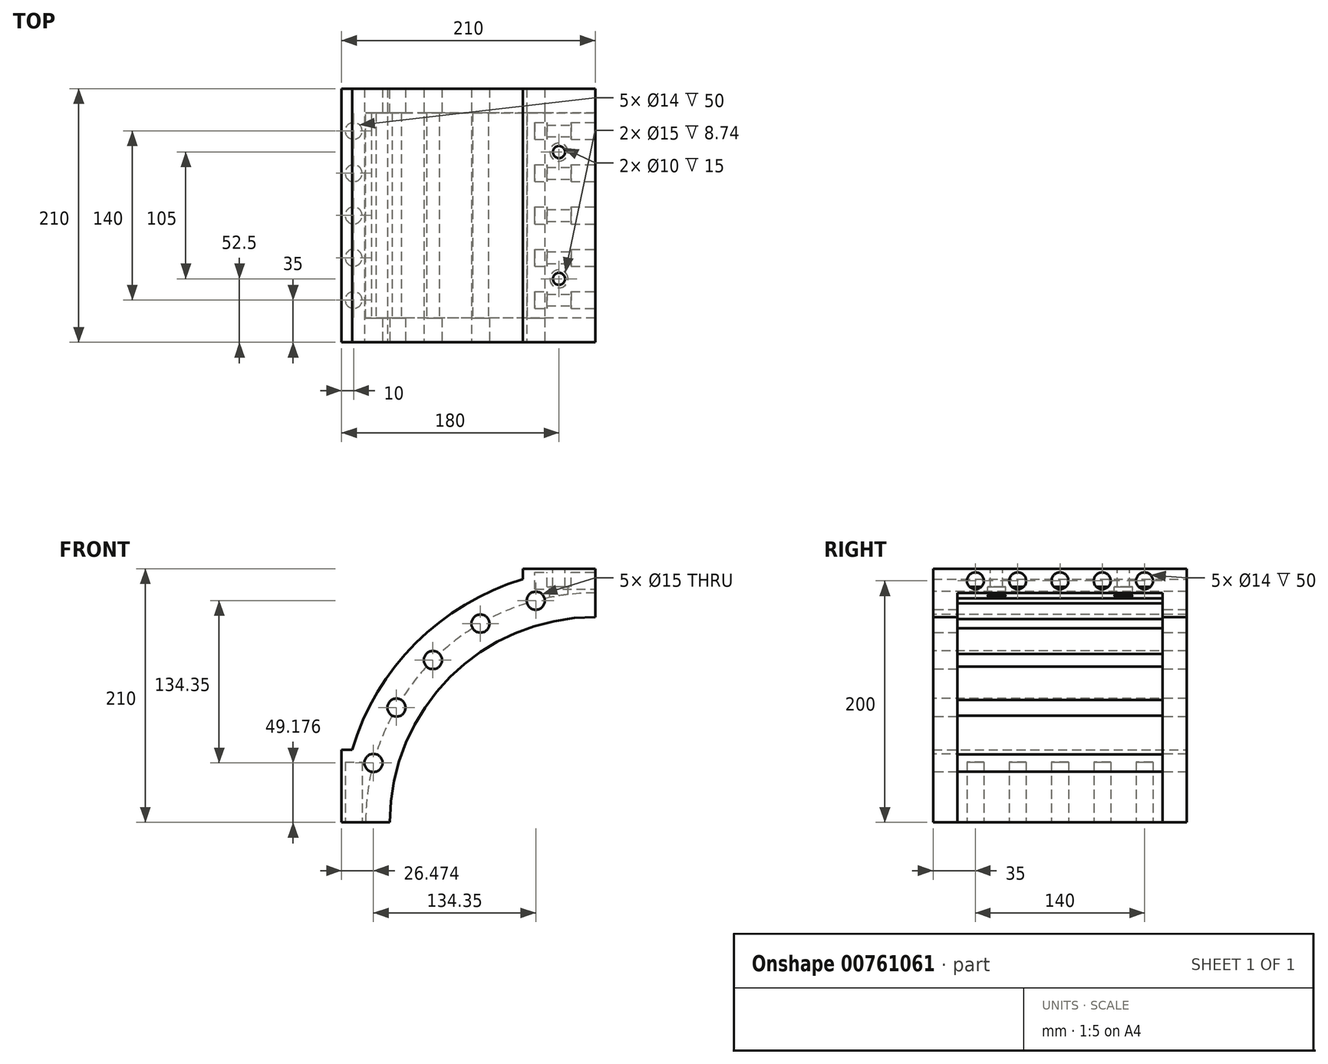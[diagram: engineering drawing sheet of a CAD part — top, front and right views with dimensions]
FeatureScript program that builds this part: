
annotation { "Feature Type Name" : "Feature", "Feature Type Description" : "" }
export const myFeature = defineFeature(function(context is Context, id is Id, definition is map)
    precondition{}
    {
        {
            var Q0;
            Q0=qCreatedBy(makeId("Front.planeOp"),FACE);
            var sketch = newSketch(context, id + "F0", { "sketchPlane" : qUnion([Q0])});
            skCircle(sketch, "E0", {"center": v(0, 0) * mm, "radius": 210 * mm});
            skCircle(sketch, "E1", {"center": v(0, 0) * mm, "radius": 190 * mm});
            skLineSegment(sketch, "E2.bottom", {"start": v(-210, 210) * mm, "end": v(210, 210) * mm});
            skLineSegment(sketch, "E2.top", {"start": v(-210, -210) * mm, "end": v(210, -210) * mm});
            skLineSegment(sketch, "E2.left", {"start": v(-210, 210) * mm, "end": v(-210, -210) * mm});
            skLineSegment(sketch, "E2.right", {"start": v(210, 210) * mm, "end": v(210, -210) * mm});
            skLineSegment(sketch, "E3", {"start": v(0, 210) * mm, "end": v(0, 0) * mm});
            skLineSegment(sketch, "E4", {"start": v(-210, 0) * mm, "end": v(0, 0) * mm});
            skSolve(sketch);
        }
        {
            var Q0;
            {var subQ0=sQuery(id+"F0.wireOp",EDGE,"E3");var subQ5=sQuery(id+"F0.wireOp",EDGE,"E1");var subQ7=makeQuery(id+"F0.imprint","INTERSECT",VERTEX,{"derivedFrom":[subQ5,subQ0]});Q0=makeQuery(id+"F0.imprint","IMPRINT",FACE,{"disambiguationData":[TD([[makeQuery(id+"F0.imprint","IMPRINT",EDGE,{"disambiguationData":[TD([[subQ7,-1.0]])],"derivedFrom":subQ5}),-1.0]])]});}
            extrude(context, id + "F1", {"entities" : qUnion([Q0]), "depth" : 210 * mm, "offsetDistance" : 25 * mm});
        }
        {
            var Q0;
            Q0=makeQuery(id+"F1.opExtrude","SWEPT_FACE",FACE,{"disambiguationData":[OSD([sQuery(id+"F0.wireOp",EDGE,"E3")])]});
            var sketch = newSketch(context, id + "F2", { "sketchPlane" : qUnion([Q0])});
            skSolve(sketch);
        }
        {
            var Q0;
            Q0 = qSketchRegion(id + "F2", true);
            var Q1;
            {var subQ0=sQuery(id+"F0.wireOp",EDGE,"E3");Q1=makeQuery(id+"F2.imprint","IMPRINT",FACE,{"disambiguationData":[TD([[makeQuery(id+"F2.imprint","IMPRINT",EDGE,{"derivedFrom":makeQuery(id+"F1.opExtrude","CAP_EDGE",EDGE,{"disambiguationData":[OSD([subQ0])],"isStart":true})}),-1.0]])]});}
            extrude(context, id + "F3", {"entities" : qUnion([Q0, Q1]), "operationType" : NewBodyOperationType.ADD, "oppositeDirection" : true, "depth" : 60 * mm, "offsetDistance" : 25 * mm});
        }
        {
            var Q0;
            Q0=makeQuery(id+"F1.opExtrude","SWEPT_FACE",FACE,{"disambiguationData":[OSD([sQuery(id+"F0.wireOp",EDGE,"E4")])]});
            extrude(context, id + "F4", {"entities" : qUnion([Q0]), "operationType" : NewBodyOperationType.ADD, "oppositeDirection" : true, "depth" : 60 * mm, "offsetDistance" : 25 * mm});
        }
        {
            var Q0;
            Q0=makeQuery(id+"F1.opExtrude","SWEPT_FACE",FACE,{"disambiguationData":[OSD([sQuery(id+"F0.wireOp",EDGE,"E3")])]});
            var sketch = newSketch(context, id + "F5", { "sketchPlane" : qUnion([Q0])});
            skLineSegment(sketch, "E5", {"start": v(-210, 200) * mm, "end": v(0, 200) * mm, "construction": true});
            skLineSegment(sketch, "E6", {"start": v(-105, 210) * mm, "end": v(-105, 190) * mm, "construction": true});
            skLineSegment(sketch, "E7", {"start": v(-175, 210) * mm, "end": v(-175, 190) * mm, "construction": true});
            skLineSegment(sketch, "E8", {"start": v(-140, 210) * mm, "end": v(-140, 190) * mm, "construction": true});
            skLineSegment(sketch, "E9", {"start": v(-70, 210) * mm, "end": v(-70, 190) * mm, "construction": true});
            skLineSegment(sketch, "E10", {"start": v(-35, 210) * mm, "end": v(-35, 190) * mm, "construction": true});
            skCircle(sketch, "E11", {"center": v(-175, 200) * mm, "radius": 7 * mm});
            skCircle(sketch, "E12", {"center": v(-140, 200) * mm, "radius": 7 * mm});
            skCircle(sketch, "E13", {"center": v(-105, 200) * mm, "radius": 7 * mm});
            skCircle(sketch, "E14", {"center": v(-70, 200) * mm, "radius": 7 * mm});
            skCircle(sketch, "E15", {"center": v(-35, 200) * mm, "radius": 7 * mm});
            skSolve(sketch);
        }
        {
            var Q0;
            Q0=makeQuery(id+"F5.imprint","IMPRINT",FACE,{"disambiguationData":[TD([[makeQuery(id+"F5.imprint","IMPRINT",EDGE,{"derivedFrom":sQuery(id+"F5.wireOp",EDGE,"E11")}),1.0]])]});
            var Q1;
            Q1=makeQuery(id+"F5.imprint","IMPRINT",FACE,{"disambiguationData":[TD([[makeQuery(id+"F5.imprint","IMPRINT",EDGE,{"derivedFrom":sQuery(id+"F5.wireOp",EDGE,"E12")}),1.0]])]});
            var Q2;
            Q2=makeQuery(id+"F5.imprint","IMPRINT",FACE,{"disambiguationData":[TD([[makeQuery(id+"F5.imprint","IMPRINT",EDGE,{"derivedFrom":sQuery(id+"F5.wireOp",EDGE,"E13")}),1.0]])]});
            var Q3;
            Q3=makeQuery(id+"F5.imprint","IMPRINT",FACE,{"disambiguationData":[TD([[makeQuery(id+"F5.imprint","IMPRINT",EDGE,{"derivedFrom":sQuery(id+"F5.wireOp",EDGE,"E14")}),1.0]])]});
            var Q4;
            Q4=makeQuery(id+"F5.imprint","IMPRINT",FACE,{"disambiguationData":[TD([[makeQuery(id+"F5.imprint","IMPRINT",EDGE,{"derivedFrom":sQuery(id+"F5.wireOp",EDGE,"E15")}),1.0]])]});
            var Q5;
            Q5 = qSketchRegion(id + "F7", true);
            extrude(context, id + "F6", {"entities" : qUnion([Q0, Q1, Q2, Q3, Q4, Q5]), "operationType" : NewBodyOperationType.REMOVE, "oppositeDirection" : true, "depth" : 50 * mm, "offsetDistance" : 25 * mm});
        }
        {
            var Q0;
            Q0=makeQuery(id+"F3.opExtrude","SWEPT_FACE",FACE,{"disambiguationData":[OSD([sQuery(id+"F0.wireOp",EDGE,"E0"),sQuery(id+"F0.wireOp",EDGE,"E2.bottom"),sQuery(id+"F0.wireOp",EDGE,"E3")])]});
            var sketch = newSketch(context, id + "F7", { "sketchPlane" : qUnion([Q0])});
            skLineSegment(sketch, "E16", {"start": v(-30, -210) * mm, "end": v(-30, 0) * mm});
            skLineSegment(sketch, "E17", {"start": v(-60, -157.5) * mm, "end": v(0, -157.5) * mm});
            skLineSegment(sketch, "E18", {"start": v(-60, -52.5) * mm, "end": v(0, -52.5) * mm});
            skLineSegment(sketch, "E19", {"start": v(-60, -105) * mm, "end": v(0, -105) * mm});
            skPoint(sketch, "E20", {"position": v(-30, -157.5) * mm});
            skPoint(sketch, "E21", {"position": v(-30, -105) * mm});
            skPoint(sketch, "E22", {"position": v(-30, -52.5) * mm});
            skSolve(sketch);
        }
        {
            var Q0;
            Q0=sQuery(id+"F7.wireOp",VERTEX,"E20");
            var Q1;
            Q1=sQuery(id+"F7.wireOp",VERTEX,"E22");
            var Q2;
            Q2=makeQuery(id+"F1.opExtrude","SWEPT_BODY",BODY,{"disambiguationData":[OSD([sQuery(id+"F0.wireOp",EDGE,"E0"),sQuery(id+"F0.wireOp",EDGE,"E1"),sQuery(id+"F0.wireOp",EDGE,"E3"),sQuery(id+"F0.wireOp",EDGE,"E4")])]});
            hole(context, id + "F8", {"style" : HoleStyle.SIMPLE, "endStyle" : HoleEndStyle.BLIND, "holeDiameter" : 15 * mm, "majorDiameter" : 5 * mm, "holeDepth" : 40 * mm, "isTappedThrough" : true, "tappedDepth" : 12 * mm, "tapClearance" : 3, "startFromSketch" : true, "locations" : qUnion([Q0, Q1]), "scope" : qUnion([Q2])});
        }
        {
            var Q0;
            {var subQ0=sQuery(id+"F0.wireOp",EDGE,"E4");var subQ1=sQuery(id+"F0.wireOp",EDGE,"E3");Q0=makeQuery(id+"F4.boolean.opBoolean","MERGE",FACE,{"derivedFrom":[makeQuery(id+"F3.boolean.opBoolean","MERGE",FACE,{"derivedFrom":[makeQuery(id+"F1.opExtrude","CAP_FACE",FACE,{"disambiguationData":[OSD([sQuery(id+"F0.wireOp",EDGE,"E0"),sQuery(id+"F0.wireOp",EDGE,"E1"),subQ1,subQ0])],"isStart":false}),makeQuery(id+"F3.opExtrude","SWEPT_FACE",FACE,{"disambiguationData":[OSD([subQ1]),TDD([makeQuery(id+"F2.imprint","IMPRINT",EDGE,{"derivedFrom":makeQuery(id+"F1.opExtrude","CAP_EDGE",EDGE,{"disambiguationData":[OSD([subQ1])],"isStart":false})})])]})]}),makeQuery(id+"F4.opExtrude","SWEPT_FACE",FACE,{"disambiguationData":[OSD([subQ0]),TDD([makeQuery(id+"F1.opExtrude","CAP_EDGE",EDGE,{"disambiguationData":[OSD([subQ0])],"isStart":false})])]})]});}
            var sketch = newSketch(context, id + "F9", { "sketchPlane" : qUnion([Q0])});
            skLineSegment(sketch, "E23", {"start": v(0, 0) * mm, "end": v(-200, 0) * mm, "construction": true});
            skCircle(sketch, "E24", {"center": v(0, 0) * mm, "radius": 170 * mm});
            skLineSegment(sketch, "E25", {"start": v(0, 0) * mm, "end": v(0, 190) * mm, "construction": true});
            skLineSegment(sketch, "E26", {"start": v(0, 190) * mm, "end": v(0, 170) * mm});
            skLineSegment(sketch, "E27", {"start": v(-190, 0) * mm, "end": v(-170, 0) * mm});
            skSolve(sketch);
        }
        {
            var Q0;
            {var subQ0=sQuery(id+"F9.wireOp",EDGE,"E26");Q0=makeQuery(id+"F9.imprint","IMPRINT",FACE,{"disambiguationData":[TD([[makeQuery(id+"F9.imprint","IMPRINT",EDGE,{"derivedFrom":subQ0}),-1.0]])]});}
            extrude(context, id + "F10", {"entities" : qUnion([Q0]), "operationType" : NewBodyOperationType.ADD, "oppositeDirection" : true, "depth" : 20 * mm, "offsetDistance" : 25 * mm});
        }
        {
            var Q0;
            {var subQ0=sQuery(id+"F0.wireOp",EDGE,"E4");var subQ1=sQuery(id+"F0.wireOp",EDGE,"E3");Q0=makeQuery(id+"F4.boolean.opBoolean","MERGE",FACE,{"derivedFrom":[makeQuery(id+"F3.boolean.opBoolean","MERGE",FACE,{"derivedFrom":[makeQuery(id+"F1.opExtrude","CAP_FACE",FACE,{"disambiguationData":[OSD([sQuery(id+"F0.wireOp",EDGE,"E0"),sQuery(id+"F0.wireOp",EDGE,"E1"),subQ1,subQ0])],"isStart":true}),makeQuery(id+"F3.opExtrude","SWEPT_FACE",FACE,{"disambiguationData":[OSD([subQ1]),TDD([makeQuery(id+"F2.imprint","IMPRINT",EDGE,{"derivedFrom":makeQuery(id+"F1.opExtrude","CAP_EDGE",EDGE,{"disambiguationData":[OSD([subQ1])],"isStart":true})})])]})]}),makeQuery(id+"F4.opExtrude","SWEPT_FACE",FACE,{"disambiguationData":[OSD([subQ0]),TDD([makeQuery(id+"F1.opExtrude","CAP_EDGE",EDGE,{"disambiguationData":[OSD([subQ0])],"isStart":true})])]})]});}
            var sketch = newSketch(context, id + "F11", { "sketchPlane" : qUnion([Q0])});
            skCircle(sketch, "E28", {"center": v(0, 0) * mm, "radius": 170 * mm});
            skLineSegment(sketch, "E29", {"start": v(0, 190) * mm, "end": v(0, 170) * mm});
            skLineSegment(sketch, "E30", {"start": v(190, 0) * mm, "end": v(170, 0) * mm});
            skSolve(sketch);
        }
        {
            var Q0;
            {var subQ0=sQuery(id+"F11.wireOp",EDGE,"E29");Q0=makeQuery(id+"F11.imprint","IMPRINT",FACE,{"disambiguationData":[TD([[makeQuery(id+"F11.imprint","IMPRINT",EDGE,{"derivedFrom":subQ0}),1.0]])]});}
            extrude(context, id + "F12", {"entities" : qUnion([Q0]), "operationType" : NewBodyOperationType.ADD, "oppositeDirection" : true, "depth" : 20 * mm, "offsetDistance" : 25 * mm});
        }
        {
            var Q0;
            {var subQ0=sQuery(id+"F0.wireOp",EDGE,"E1");var subQ1=sQuery(id+"F0.wireOp",EDGE,"E4");var subQ2=sQuery(id+"F0.wireOp",EDGE,"E3");Q0=makeQuery(id+"F10.boolean.opBoolean","MERGE",FACE,{"derivedFrom":[makeQuery(id+"F4.boolean.opBoolean","MERGE",FACE,{"derivedFrom":[makeQuery(id+"F3.boolean.opBoolean","MERGE",FACE,{"derivedFrom":[makeQuery(id+"F1.opExtrude","CAP_FACE",FACE,{"disambiguationData":[OSD([sQuery(id+"F0.wireOp",EDGE,"E0"),subQ0,subQ2,subQ1])],"isStart":false}),makeQuery(id+"F3.opExtrude","SWEPT_FACE",FACE,{"disambiguationData":[OSD([subQ2]),TDD([makeQuery(id+"F2.imprint","IMPRINT",EDGE,{"derivedFrom":makeQuery(id+"F1.opExtrude","CAP_EDGE",EDGE,{"disambiguationData":[OSD([subQ2])],"isStart":false})})])]})]}),makeQuery(id+"F4.opExtrude","SWEPT_FACE",FACE,{"disambiguationData":[OSD([subQ1]),TDD([makeQuery(id+"F1.opExtrude","CAP_EDGE",EDGE,{"disambiguationData":[OSD([subQ1])],"isStart":false})])]})]}),makeQuery(id+"F10.opExtrude","CAP_FACE",FACE,{"disambiguationData":[OSD([subQ0,sQuery(id+"F9.wireOp",EDGE,"E24"),sQuery(id+"F9.wireOp",EDGE,"E26"),sQuery(id+"F9.wireOp",EDGE,"E27")])],"isStart":true})]});}
            var sketch = newSketch(context, id + "F13", { "sketchPlane" : qUnion([Q0])});
            skPoint(sketch, "E31", {"position": v(0, 190) * mm});
            skCircle(sketch, "E32", {"center": v(0, 0) * mm, "radius": 190 * mm});
            skLineSegment(sketch, "E33", {"start": v(0, 0) * mm, "end": v(0, 190) * mm, "construction": true});
            skLineSegment(sketch, "E34", {"start": v(0, 0) * mm, "end": v(-190, 0) * mm, "construction": true});
            skLineSegment(sketch, "E35", {"start": v(0, 0) * mm, "end": v(-164.54, 95) * mm, "construction": true});
            skLineSegment(sketch, "E36", {"start": v(0, 0) * mm, "end": v(-95, 164.54) * mm, "construction": true});
            skLineSegment(sketch, "E37", {"start": v(0, 0) * mm, "end": v(-49.18, 183.53) * mm, "construction": true});
            skLineSegment(sketch, "E38", {"start": v(0, 0) * mm, "end": v(-183.53, 49.18) * mm, "construction": true});
            skLineSegment(sketch, "E39", {"start": v(0, 0) * mm, "end": v(-134.35, 134.35) * mm, "construction": true});
            skPoint(sketch, "E40", {"position": v(-49.18, 183.53) * mm});
            skPoint(sketch, "E41", {"position": v(-95, 164.54) * mm});
            skPoint(sketch, "E42", {"position": v(-134.35, 134.35) * mm});
            skPoint(sketch, "E43", {"position": v(-164.54, 95) * mm});
            skPoint(sketch, "E44", {"position": v(-183.53, 49.18) * mm});
            skSolve(sketch);
        }
        {
            var Q0;
            Q0=sQuery(id+"F13.wireOp",VERTEX,"E44");
            var Q1;
            Q1=sQuery(id+"F13.wireOp",VERTEX,"E43");
            var Q2;
            Q2=sQuery(id+"F13.wireOp",VERTEX,"E42");
            var Q3;
            Q3=sQuery(id+"F13.wireOp",VERTEX,"E41");
            var Q4;
            Q4=sQuery(id+"F13.wireOp",VERTEX,"E40");
            var Q5;
            Q5=makeQuery(id+"F1.opExtrude","SWEPT_BODY",BODY,{"disambiguationData":[OSD([sQuery(id+"F0.wireOp",EDGE,"E0"),sQuery(id+"F0.wireOp",EDGE,"E1"),sQuery(id+"F0.wireOp",EDGE,"E3"),sQuery(id+"F0.wireOp",EDGE,"E4")])]});
            hole(context, id + "F14", {"style" : HoleStyle.SIMPLE, "endStyle" : HoleEndStyle.BLIND, "holeDiameter" : 15 * mm, "majorDiameter" : 5 * mm, "holeDepth" : 220 * mm, "isTappedThrough" : true, "tappedDepth" : 12 * mm, "tapClearance" : 3, "startFromSketch" : true, "locations" : qUnion([Q0, Q1, Q2, Q3, Q4]), "scope" : qUnion([Q5])});
        }
        {
            var Q0;
            {var subQ0=sQuery(id+"F0.wireOp",EDGE,"E1");var subQ1=sQuery(id+"F0.wireOp",EDGE,"E4");var subQ2=sQuery(id+"F0.wireOp",EDGE,"E3");Q0=makeQuery(id+"F12.boolean.opBoolean","MERGE",FACE,{"derivedFrom":[makeQuery(id+"F4.boolean.opBoolean","MERGE",FACE,{"derivedFrom":[makeQuery(id+"F3.boolean.opBoolean","MERGE",FACE,{"derivedFrom":[makeQuery(id+"F1.opExtrude","CAP_FACE",FACE,{"disambiguationData":[OSD([sQuery(id+"F0.wireOp",EDGE,"E0"),subQ0,subQ2,subQ1])],"isStart":true}),makeQuery(id+"F3.opExtrude","SWEPT_FACE",FACE,{"disambiguationData":[OSD([subQ2]),TDD([makeQuery(id+"F2.imprint","IMPRINT",EDGE,{"derivedFrom":makeQuery(id+"F1.opExtrude","CAP_EDGE",EDGE,{"disambiguationData":[OSD([subQ2])],"isStart":true})})])]})]}),makeQuery(id+"F4.opExtrude","SWEPT_FACE",FACE,{"disambiguationData":[OSD([subQ1]),TDD([makeQuery(id+"F1.opExtrude","CAP_EDGE",EDGE,{"disambiguationData":[OSD([subQ1])],"isStart":true})])]})]}),makeQuery(id+"F12.opExtrude","CAP_FACE",FACE,{"disambiguationData":[OSD([subQ0,sQuery(id+"F11.wireOp",EDGE,"E28"),sQuery(id+"F11.wireOp",EDGE,"E29"),sQuery(id+"F11.wireOp",EDGE,"E30")])],"isStart":true})]});}
            var sketch = newSketch(context, id + "F15", { "sketchPlane" : qUnion([Q0])});
            skLineSegment(sketch, "E45", {"start": v(30, 210) * mm, "end": v(30, 167.33) * mm, "construction": true});
            skLineSegment(sketch, "E46", {"start": v(20, 210) * mm, "end": v(20, 168.82) * mm});
            skLineSegment(sketch, "E47", {"start": v(40, 210) * mm, "end": v(40, 165.23) * mm});
            skLineSegment(sketch, "E48", {"start": v(20, 190) * mm, "end": v(40, 190) * mm});
            skLineSegment(sketch, "E49", {"start": v(40, 195) * mm, "end": v(20, 195) * mm});
            skSolve(sketch);
        }
        {
            var Q0;
            {var subQ6=sQuery(id+"F15.wireOp",EDGE,"E49");Q0=makeQuery(id+"F15.imprint","IMPRINT",FACE,{"disambiguationData":[TD([[makeQuery(id+"F15.imprint","IMPRINT",EDGE,{"derivedFrom":subQ6}),-1.0]])]});}
            extrude(context, id + "F16", {"entities" : qUnion([Q0]), "operationType" : NewBodyOperationType.ADD, "oppositeDirection" : true, "depth" : 200 * mm, "offsetDistance" : 25 * mm});
        }
        {
            var Q0;
            Q0=sQuery(id+"F7.wireOp",VERTEX,"E22");
            var Q1;
            Q1=sQuery(id+"F7.wireOp",VERTEX,"E20");
            var Q2;
            Q2=makeQuery(id+"F1.opExtrude","SWEPT_BODY",BODY,{"disambiguationData":[OSD([sQuery(id+"F0.wireOp",EDGE,"E0"),sQuery(id+"F0.wireOp",EDGE,"E1"),sQuery(id+"F0.wireOp",EDGE,"E3"),sQuery(id+"F0.wireOp",EDGE,"E4")])]});
            hole(context, id + "F17", {"style" : HoleStyle.SIMPLE, "endStyle" : HoleEndStyle.BLIND, "holeDiameter" : 10 * mm, "majorDiameter" : 5 * mm, "holeDepth" : 40 * mm, "isTappedThrough" : true, "tappedDepth" : 12 * mm, "tapClearance" : 3, "startFromSketch" : true, "locations" : qUnion([Q0, Q1]), "scope" : qUnion([Q2])});
        }
        {
            var Q0;
            Q0=makeQuery(id+"F12.boolean.opBoolean","MERGE",FACE,{"derivedFrom":[makeQuery(id+"F10.boolean.opBoolean","MERGE",FACE,{"derivedFrom":[makeQuery(id+"F1.opExtrude","SWEPT_FACE",FACE,{"disambiguationData":[OSD([sQuery(id+"F0.wireOp",EDGE,"E4")])]}),makeQuery(id+"F10.opExtrude","SWEPT_FACE",FACE,{"disambiguationData":[OSD([sQuery(id+"F9.wireOp",EDGE,"E27")])]})]}),makeQuery(id+"F12.opExtrude","SWEPT_FACE",FACE,{"disambiguationData":[OSD([sQuery(id+"F11.wireOp",EDGE,"E30")])]})]});
            var sketch = newSketch(context, id + "F18", { "sketchPlane" : qUnion([Q0])});
            skLineSegment(sketch, "E50", {"start": v(-190, 105) * mm, "end": v(-210, 105) * mm, "construction": true});
            skLineSegment(sketch, "E51", {"start": v(-200, 105) * mm, "end": v(-200, 210) * mm, "construction": true});
            skLineSegment(sketch, "E52", {"start": v(-200, 105) * mm, "end": v(-200, 0) * mm, "construction": true});
            skLineSegment(sketch, "E53", {"start": v(-210, 35) * mm, "end": v(-190, 35) * mm, "construction": true});
            skLineSegment(sketch, "E54", {"start": v(-210, 70) * mm, "end": v(-190, 70) * mm, "construction": true});
            skLineSegment(sketch, "E55", {"start": v(-210, 175) * mm, "end": v(-190, 175) * mm, "construction": true});
            skLineSegment(sketch, "E56", {"start": v(-210, 140) * mm, "end": v(-190, 140) * mm, "construction": true});
            skPoint(sketch, "E57", {"position": v(-200, 35) * mm});
            skPoint(sketch, "E58", {"position": v(-200, 70) * mm});
            skPoint(sketch, "E59", {"position": v(-200, 105) * mm});
            skPoint(sketch, "E60", {"position": v(-200, 140) * mm});
            skPoint(sketch, "E61", {"position": v(-200, 175) * mm});
            skCircle(sketch, "E62", {"center": v(-200, 35) * mm, "radius": 7 * mm});
            skCircle(sketch, "E63", {"center": v(-200, 70) * mm, "radius": 7 * mm});
            skCircle(sketch, "E64", {"center": v(-200, 105) * mm, "radius": 7 * mm});
            skCircle(sketch, "E65", {"center": v(-200, 140) * mm, "radius": 7 * mm});
            skCircle(sketch, "E66", {"center": v(-200, 175) * mm, "radius": 7 * mm});
            skSolve(sketch);
        }
        {
            var Q0;
            Q0=makeQuery(id+"F18.imprint","IMPRINT",FACE,{"disambiguationData":[TD([[makeQuery(id+"F18.imprint","IMPRINT",EDGE,{"derivedFrom":sQuery(id+"F18.wireOp",EDGE,"E62")}),1.0]])]});
            var Q1;
            Q1=makeQuery(id+"F18.imprint","IMPRINT",FACE,{"disambiguationData":[TD([[makeQuery(id+"F18.imprint","IMPRINT",EDGE,{"derivedFrom":sQuery(id+"F18.wireOp",EDGE,"E63")}),1.0]])]});
            var Q2;
            Q2=makeQuery(id+"F18.imprint","IMPRINT",FACE,{"disambiguationData":[TD([[makeQuery(id+"F18.imprint","IMPRINT",EDGE,{"derivedFrom":sQuery(id+"F18.wireOp",EDGE,"E64")}),1.0]])]});
            var Q3;
            Q3=makeQuery(id+"F18.imprint","IMPRINT",FACE,{"disambiguationData":[TD([[makeQuery(id+"F18.imprint","IMPRINT",EDGE,{"derivedFrom":sQuery(id+"F18.wireOp",EDGE,"E65")}),1.0]])]});
            var Q4;
            Q4=makeQuery(id+"F18.imprint","IMPRINT",FACE,{"disambiguationData":[TD([[makeQuery(id+"F18.imprint","IMPRINT",EDGE,{"derivedFrom":sQuery(id+"F18.wireOp",EDGE,"E66")}),1.0]])]});
            extrude(context, id + "F19", {"entities" : qUnion([Q0, Q1, Q2, Q3, Q4]), "operationType" : NewBodyOperationType.REMOVE, "oppositeDirection" : true, "depth" : 50 * mm, "offsetDistance" : 25 * mm});
        }
    });
